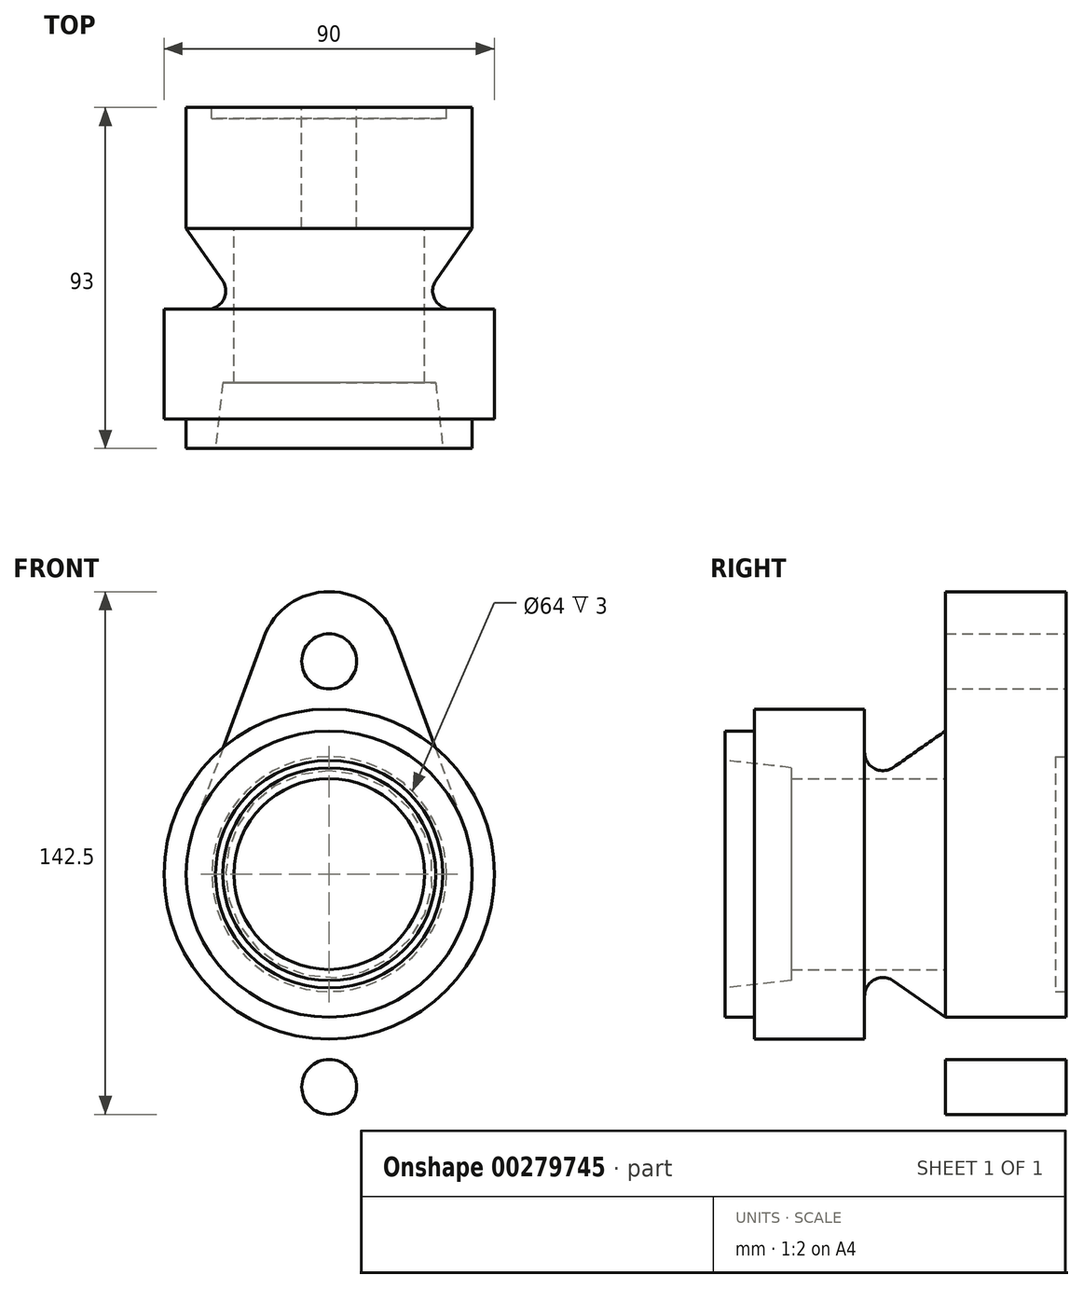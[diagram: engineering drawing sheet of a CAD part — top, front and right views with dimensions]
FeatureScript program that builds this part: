
annotation { "Feature Type Name" : "Feature", "Feature Type Description" : "" }
export const myFeature = defineFeature(function(context is Context, id is Id, definition is map)
    precondition{}
    {
        {
            var Q0;
            Q0=qCreatedBy(makeId("Right.planeOp"),FACE);
            var sketch = newSketch(context, id + "F0", { "sketchPlane" : qUnion([Q0])});
            skLineSegment(sketch, "E0", {"start": v(-60, 31) * mm, "end": v(-60, 39) * mm});
            skLineSegment(sketch, "E1", {"start": v(-60, 39) * mm, "end": v(-52, 39) * mm});
            skLineSegment(sketch, "E2", {"start": v(-52, 39) * mm, "end": v(-52, 45) * mm});
            skLineSegment(sketch, "E3", {"start": v(-52, 45) * mm, "end": v(-22, 45) * mm});
            skLineSegment(sketch, "E4", {"start": v(-22, 45) * mm, "end": v(-22, 33.2) * mm});
            skLineSegment(sketch, "E5", {"start": v(-14.13, 29.1) * mm, "end": v(0, 39) * mm});
            skLineSegment(sketch, "E6", {"start": v(0, 39) * mm, "end": v(33, 39) * mm});
            skLineSegment(sketch, "E7", {"start": v(33, 39) * mm, "end": v(33, 32) * mm});
            skLineSegment(sketch, "E8", {"start": v(33, 32) * mm, "end": v(30, 32) * mm});
            skLineSegment(sketch, "E9", {"start": v(30, 32) * mm, "end": v(30, 0) * mm});
            skLineSegment(sketch, "E10", {"start": v(30, 0) * mm, "end": v(0, 0) * mm});
            skLineSegment(sketch, "E11", {"start": v(0, 0) * mm, "end": v(0, 26) * mm});
            skLineSegment(sketch, "E12", {"start": v(0, 26) * mm, "end": v(-42, 26) * mm});
            skLineSegment(sketch, "E13", {"start": v(-42, 26) * mm, "end": v(-42, 29) * mm});
            skLineSegment(sketch, "E14", {"start": v(-42, 29) * mm, "end": v(-60, 31) * mm});
            skPoint(sketch, "E15.visualSharp", {"position": v(-22, 23.6) * mm});
            skArc(sketch, "E15.filletArc", {"start": v(-22, 33.2) * mm, "mid": v(-19.3, 28.77) * mm, "end": v(-14.13, 29.1) * mm});
            skSolve(sketch);
        }
        {
            var Q0;
            Q0=makeQuery(id+"F0.imprint","IMPRINT",FACE,{"disambiguationData":[TD([[makeQuery(id+"F0.imprint","IMPRINT",EDGE,{"derivedFrom":sQuery(id+"F0.wireOp",EDGE,"E0")}),-1.0]])]});
            var Q1;
            Q1=sQuery(id+"F0.wireOp",EDGE,"E10");
            revolve(context, id + "F1", {"entities" : qUnion([Q0]), "axis" : qUnion([Q1]), "revolveType" : RevolveType.FULL});
        }
        {
            var Q0;
            Q0=makeQuery(id+"F1.opRevolve","SWEPT_FACE",FACE,{"disambiguationData":[OSD([sQuery(id+"F0.wireOp",EDGE,"E7")])]});
            var sketch = newSketch(context, id + "F2", { "sketchPlane" : qUnion([Q0])});
            skLineSegment(sketch, "E16", {"start": v(0, 0) * mm, "end": v(0, 89.62) * mm, "construction": true});
            skLineSegment(sketch, "E17", {"start": v(22.16, 58) * mm, "end": v(-20.73, 58) * mm, "construction": true});
            skCircle(sketch, "E18", {"center": v(0, 58) * mm, "radius": 7.5 * mm});
            skArc(sketch, "E19", {"start": v(17.83, 64.55) * mm, "mid": v(0, 77) * mm, "end": v(-17.83, 64.55) * mm});
            skLineSegment(sketch, "E20", {"start": v(-17.83, 64.55) * mm, "end": v(-20.24, 58) * mm});
            skLineSegment(sketch, "E21", {"start": v(17.83, 64.55) * mm, "end": v(20.24, 58) * mm});
            skLineSegment(sketch, "E22", {"start": v(0, 0) * mm, "end": v(74.68, 0) * mm, "construction": true});
            skCircle(sketch, "E23", {"center": v(0, 0) * mm, "radius": 39 * mm});
            skLineSegment(sketch, "E24", {"start": v(20.24, 58) * mm, "end": v(36.6, 13.45) * mm});
            skLineSegment(sketch, "E25", {"start": v(-20.24, 58) * mm, "end": v(-36.6, 13.45) * mm});
            skCircle(sketch, "E26.MirrorC", {"center": v(0, -58) * mm, "radius": 7.5 * mm});
            skLineSegment(sketch, "E27.MirrorCS", {"start": v(22.16, -58) * mm, "end": v(-20.73, -58) * mm, "construction": true});
            skArc(sketch, "E28.MirrorCS", {"start": v(17.83, -64.55) * mm, "mid": v(0, -77) * mm, "end": v(-17.83, -64.55) * mm});
            skLineSegment(sketch, "E29.MirrorCS", {"start": v(-17.83, -64.55) * mm, "end": v(-20.24, -58) * mm});
            skLineSegment(sketch, "E30.MirrorCS", {"start": v(-20.24, -58) * mm, "end": v(-36.6, -13.45) * mm});
            skLineSegment(sketch, "E31.MirrorCS", {"start": v(20.24, -58) * mm, "end": v(36.6, -13.45) * mm});
            skLineSegment(sketch, "E32.MirrorCS", {"start": v(17.83, -64.55) * mm, "end": v(20.24, -58) * mm});
            skSolve(sketch);
        }
        {
            var Q0;
            Q0=makeQuery(id+"F2.imprint","IMPRINT",FACE,{"disambiguationData":[TD([[makeQuery(id+"F2.imprint","IMPRINT",EDGE,{"derivedFrom":sQuery(id+"F2.wireOp",EDGE,"E18")}),-1.0]])]});
            var Q1;
            Q1=makeQuery(id+"F2.imprint","IMPRINT",FACE,{"disambiguationData":[TD([[makeQuery(id+"F2.imprint","IMPRINT",EDGE,{"derivedFrom":sQuery(id+"F2.wireOp",EDGE,"E26.MirrorC")}),1.0]])]});
            extrude(context, id + "F3", {"entities" : qUnion([Q0, Q1]), "operationType" : NewBodyOperationType.ADD, "oppositeDirection" : true, "depth" : 33 * mm});
        }
    });
